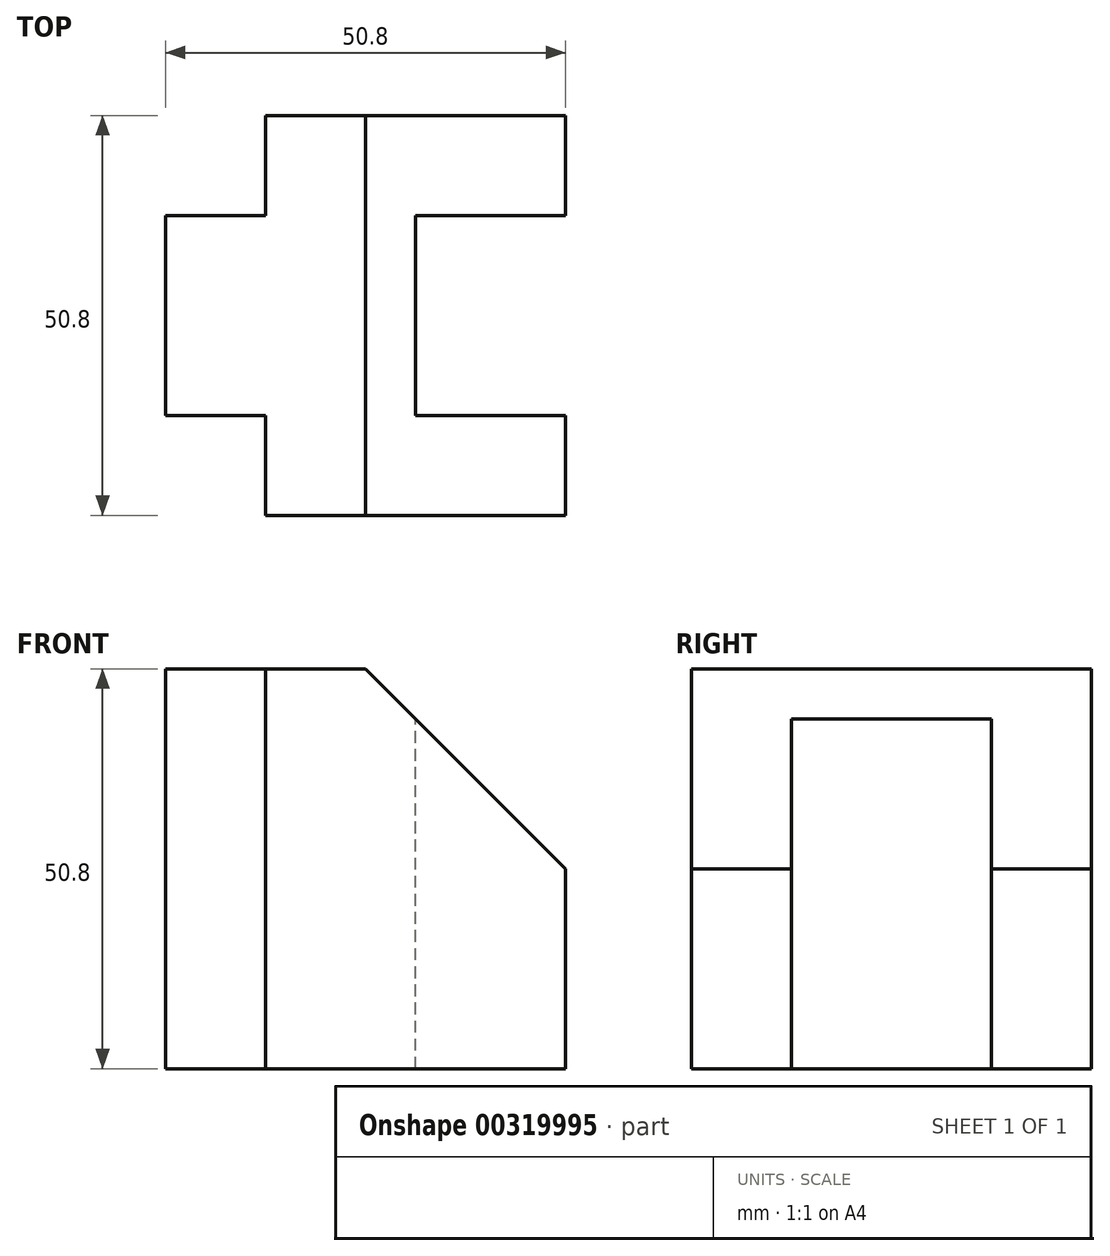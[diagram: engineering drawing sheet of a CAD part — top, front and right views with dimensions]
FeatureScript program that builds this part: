
annotation { "Feature Type Name" : "Feature", "Feature Type Description" : "" }
export const myFeature = defineFeature(function(context is Context, id is Id, definition is map)
    precondition{}
    {
        {
            var Q0;
            Q0=qCreatedBy(makeId("Top.planeOp"),FACE);
            var sketch = newSketch(context, id + "F0", { "sketchPlane" : qUnion([Q0])});
            skLineSegment(sketch, "E0.bottom", {"start": v(0, 0) * mm, "end": v(50.8, 0) * mm});
            skLineSegment(sketch, "E0.top", {"start": v(0, 50.8) * mm, "end": v(50.8, 50.8) * mm});
            skLineSegment(sketch, "E0.left", {"start": v(0, 0) * mm, "end": v(0, 50.8) * mm});
            skLineSegment(sketch, "E0.right", {"start": v(50.8, 0) * mm, "end": v(50.8, 50.8) * mm});
            skSolve(sketch);
        }
        {
            var Q0;
            Q0 = qSketchRegion(id + "F0", true);
            extrude(context, id + "F1", {"entities" : qUnion([Q0]), "depth" : 50.8 * mm});
        }
        {
            var Q0;
            Q0=makeQuery(id+"F1.opExtrude","CAP_FACE",FACE,{"disambiguationData":[OSD([sQuery(id+"F0.wireOp",EDGE,"E0.bottom"),sQuery(id+"F0.wireOp",EDGE,"E0.top"),sQuery(id+"F0.wireOp",EDGE,"E0.left"),sQuery(id+"F0.wireOp",EDGE,"E0.right")])],"isStart":false});
            var sketch = newSketch(context, id + "F2", { "sketchPlane" : qUnion([Q0])});
            skLineSegment(sketch, "E1.bottom", {"start": v(0, 38.1) * mm, "end": v(12.7, 38.1) * mm});
            skLineSegment(sketch, "E1.top", {"start": v(0, 12.7) * mm, "end": v(12.7, 12.7) * mm});
            skLineSegment(sketch, "E1.left", {"start": v(0, 38.1) * mm, "end": v(0, 12.7) * mm});
            skLineSegment(sketch, "E2", {"start": v(12.7, 38.1) * mm, "end": v(12.7, 50.8) * mm});
            skLineSegment(sketch, "E3", {"start": v(0, 38.1) * mm, "end": v(0, 50.8) * mm});
            skLineSegment(sketch, "E4", {"start": v(0, 50.8) * mm, "end": v(12.7, 50.8) * mm});
            skLineSegment(sketch, "E5", {"start": v(0, 12.7) * mm, "end": v(0, 0) * mm});
            skLineSegment(sketch, "E6", {"start": v(12.7, 12.7) * mm, "end": v(12.7, 0) * mm});
            skLineSegment(sketch, "E7", {"start": v(0, 0) * mm, "end": v(12.7, 0) * mm});
            skSolve(sketch);
        }
        {
            var Q0;
            Q0 = qSketchRegion(id + "F2", true);
            extrude(context, id + "F3", {"entities" : qUnion([Q0]), "operationType" : NewBodyOperationType.REMOVE, "oppositeDirection" : true, "depth" : 50.8 * mm});
        }
        {
            var Q0;
            Q0=makeQuery(id+"F1.opExtrude","SWEPT_FACE",FACE,{"disambiguationData":[OSD([sQuery(id+"F0.wireOp",EDGE,"E0.right")])]});
            var sketch = newSketch(context, id + "F4", { "sketchPlane" : qUnion([Q0])});
            skLineSegment(sketch, "E8.bottom", {"start": v(12.7, 0) * mm, "end": v(38.1, 0) * mm});
            skLineSegment(sketch, "E8.top", {"start": v(12.7, 50.8) * mm, "end": v(38.1, 50.8) * mm});
            skLineSegment(sketch, "E8.left", {"start": v(12.7, 0) * mm, "end": v(12.7, 50.8) * mm});
            skLineSegment(sketch, "E8.right", {"start": v(38.1, 0) * mm, "end": v(38.1, 50.8) * mm});
            skSolve(sketch);
        }
        {
            var Q0;
            Q0 = qSketchRegion(id + "F4", true);
            extrude(context, id + "F5", {"entities" : qUnion([Q0]), "operationType" : NewBodyOperationType.REMOVE, "oppositeDirection" : true, "depth" : 19.05 * mm});
        }
        {
            var Q0;
            Q0=makeQuery(id+"F1.opExtrude","SWEPT_FACE",FACE,{"disambiguationData":[OSD([sQuery(id+"F0.wireOp",EDGE,"E0.bottom")])]});
            var sketch = newSketch(context, id + "F6", { "sketchPlane" : qUnion([Q0])});
            skLineSegment(sketch, "E9", {"start": v(25.4, 50.8) * mm, "end": v(50.8, 25.4) * mm});
            skLineSegment(sketch, "E10", {"start": v(25.4, 50.8) * mm, "end": v(50.8, 50.8) * mm});
            skLineSegment(sketch, "E11", {"start": v(50.8, 50.8) * mm, "end": v(50.8, 25.4) * mm});
            skSolve(sketch);
        }
        {
            var Q0;
            Q0 = qSketchRegion(id + "F6", true);
            extrude(context, id + "F7", {"entities" : qUnion([Q0]), "operationType" : NewBodyOperationType.REMOVE, "oppositeDirection" : true, "depth" : 50.8 * mm});
        }
    });
